# Revit family: MH-X01
name_source: partatom
category: Plumbing Fixtures
revit_build: Autodesk Revit 2015 (Build: 20140322_1515(x64)
units: mm (PartAtom-declared; Revit-internal decimal feet)

## types (4) — shared parameters
Default Elevation = 48"
Manufacturer = MIFAB

MIFAB
MIFAB
R bottom = 1 3/8"
R1 = 3/16"
SC1 = 3/16"
SC2 = 1/8"
URL = www.mifab.com
id3 = 1/8"
r2 = 3/4"

## per-type parameters (varying)
| type | A | A' | B | B' | B01 | C | C' | C'1 | D | Description | PIPE SIZE | PIPE SIZE' | RP1 | RP2 | id1 | linearL | linearW | max dia | od1 | od2 | od3 |
| MH-301 | 13" | 6 1/2" | 11 3/4" | 5 7/8" | 5 1/2" | 7 5/16" | 3 5/8" | 4 1/16" | 3 1/8" | 3" HydroMax Siphonic Overflow Roof Drain | 2 15/16" | 1 1/2" | 3/16" | 3/16" | 3/16" | 1" | 2 1/8" | 3/8" | 3/8" | 5/16" | 3/16" |
| MH-401 | 19 3/8" | 9 11/16" | 17 13/16" | 8 15/16" | 8 1/2" | 10 11/16" | 5 5/16" | 5 3/4" | 3 9/16" | 4" HydroMax Siphonic Overflow Roof Drain | 3 15/16" | 1 15/16" | 3/16" | 3/16" | 3/16" | 1 5/8" | 3 9/16" | 9/16" | 3/8" | 5/16" | 3/16" |
| MH-501 | 19 3/8" | 9 11/16" | 17 13/16" | 8 15/16" | 8 7/16" | 12 3/16" | 6 1/8" | 6 1/2" | 4 5/16" | 5" HydroMax Siphonic Overflow Roof Drain | 4 15/16" | 2 7/16" | 3/16" | 1/4" | 1/4" | 1 13/16" | 3 15/16" | 9/16" | 1/2" | 3/8" | 3/16" |
| MH-601 | 25 3/16" | 12 5/8" | 22 5/16" | 11 1/8" | 10 9/16" | 15 9/16" | 7 3/4" | 8 3/16" | 4 3/4" | 6" HydroMax Siphonic Overflow Roof Drain | 5 7/8" | 2 15/16" | 1/4" | 1/4" | 1/4" | 2 9/16" | 5 1/2" | 1 1/4" | 9/16" | 1/2" | 1/4" |

note: column(s) folded — value = type name in every type: Model

## geometry (parser evidence)
native form markers: Sweep x2
no freeform markers — native parametric forms only
